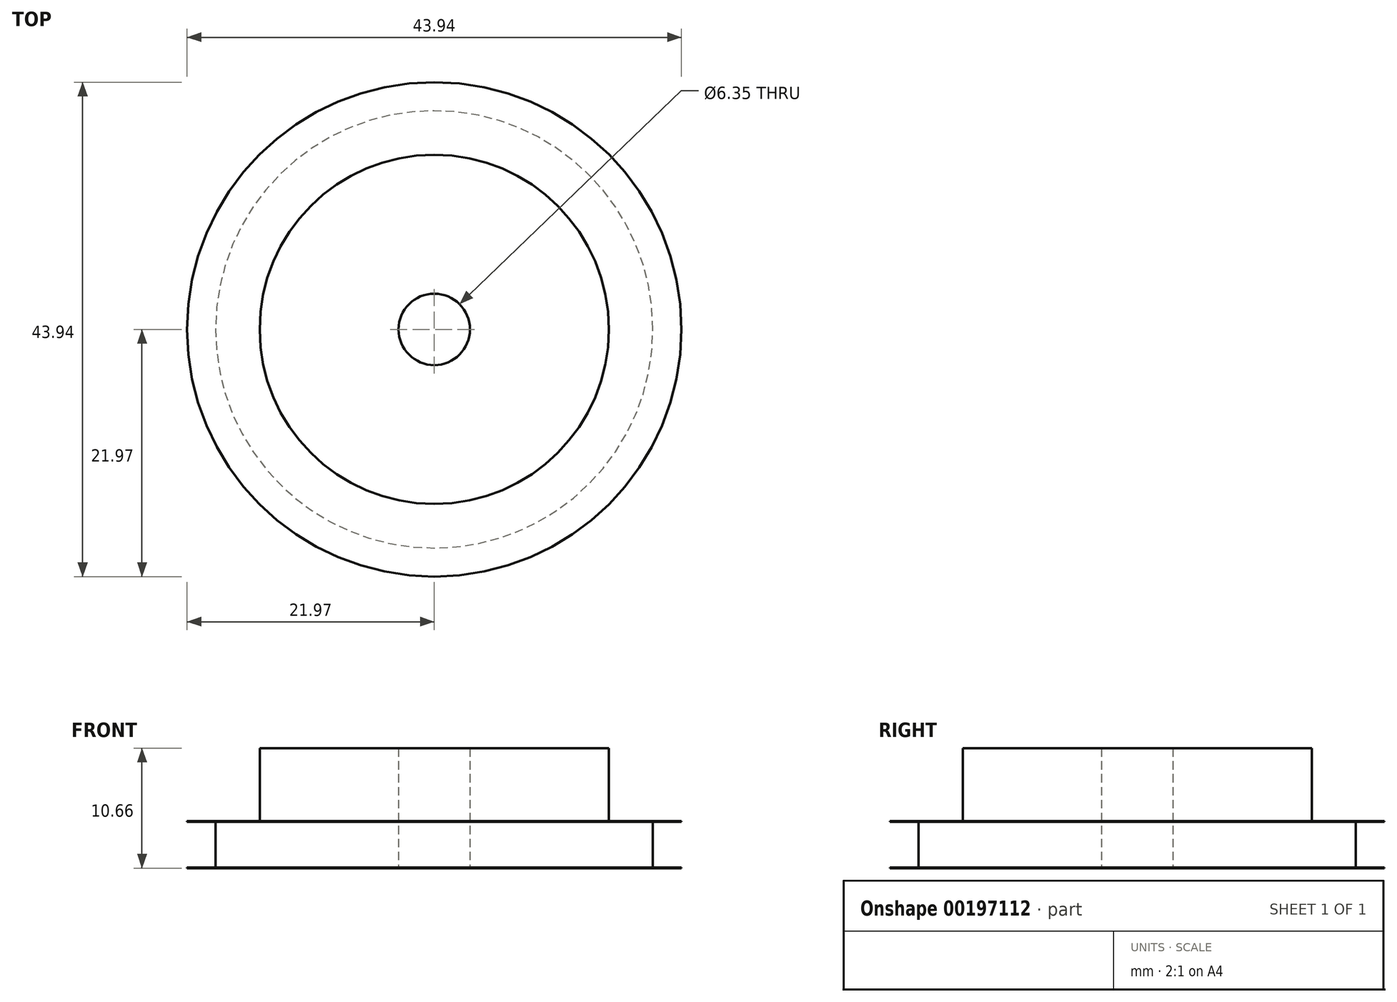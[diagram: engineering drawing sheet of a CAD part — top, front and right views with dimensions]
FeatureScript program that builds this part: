
annotation { "Feature Type Name" : "Feature", "Feature Type Description" : "" }
export const myFeature = defineFeature(function(context is Context, id is Id, definition is map)
    precondition{}
    {
        {
            var Q0;
            Q0=qCreatedBy(makeId("Top.planeOp"),FACE);
            var sketch = newSketch(context, id + "F0", { "sketchPlane" : qUnion([Q0])});
            skCircle(sketch, "E0", {"center": v(0, 0) * mm, "radius": 21.97 * mm});
            skSolve(sketch);
        }
        {
            var Q0;
            Q0 = qSketchRegion(id + "F0", true);
            extrude(context, id + "F1", {"entities" : qUnion([Q0]), "depth" : ((0.28 - 0.16) / 2) * mm});
        }
        {
            var Q0;
            Q0=makeQuery(id+"F1.opExtrude","CAP_FACE",FACE,{"disambiguationData":[OSD([sQuery(id+"F0.wireOp",EDGE,"E0")])],"isStart":false});
            var sketch = newSketch(context, id + "F2", { "sketchPlane" : qUnion([Q0])});
            skCircle(sketch, "E1", {"center": v(0, 0) * mm, "radius": 19.43 * mm});
            skSolve(sketch);
        }
        {
            var Q0;
            Q0 = qSketchRegion(id + "F2", true);
            extrude(context, id + "F3", {"entities" : qUnion([Q0]), "operationType" : NewBodyOperationType.ADD, "depth" : 4.06 * mm});
        }
        {
            var Q0;
            Q0=makeQuery(id+"F3.opExtrude","CAP_FACE",FACE,{"disambiguationData":[OSD([sQuery(id+"F2.wireOp",EDGE,"E1")])],"isStart":false});
            var sketch = newSketch(context, id + "F4", { "sketchPlane" : qUnion([Q0])});
            skCircle(sketch, "E2", {"center": v(0, 0) * mm, "radius": 21.97 * mm});
            skSolve(sketch);
        }
        {
            var Q0;
            Q0 = qSketchRegion(id + "F4", true);
            extrude(context, id + "F5", {"entities" : qUnion([Q0]), "operationType" : NewBodyOperationType.ADD, "depth" : ((0.28 - 0.16) / 2) * mm});
        }
        {
            var Q0;
            Q0=makeQuery(id+"F5.opExtrude","CAP_FACE",FACE,{"disambiguationData":[OSD([sQuery(id+"F4.wireOp",EDGE,"E2")])],"isStart":false});
            var sketch = newSketch(context, id + "F6", { "sketchPlane" : qUnion([Q0])});
            skCircle(sketch, "E3", {"center": v(0, 0) * mm, "radius": 15.52 * mm});
            skSolve(sketch);
        }
        {
            var Q0;
            Q0 = qSketchRegion(id + "F6", true);
            extrude(context, id + "F7", {"entities" : qUnion([Q0]), "operationType" : NewBodyOperationType.ADD, "depth" : 6.48 * mm});
        }
        {
            var Q0;
            Q0=makeQuery(id+"F1.opExtrude","CAP_FACE",FACE,{"disambiguationData":[OSD([sQuery(id+"F0.wireOp",EDGE,"E0")])],"isStart":true});
            var sketch = newSketch(context, id + "F8", { "sketchPlane" : qUnion([Q0])});
            skCircle(sketch, "E4", {"center": v(0, 0) * mm, "radius": 3.18 * mm});
            skSolve(sketch);
        }
        {
            var Q0;
            Q0 = qSketchRegion(id + "F8", true);
            extrude(context, id + "F9", {"entities" : qUnion([Q0]), "operationType" : NewBodyOperationType.REMOVE, "endBound" : BoundingType.THROUGH_ALL, "oppositeDirection" : true, "depth" : 25.4 * mm});
        }
    });
